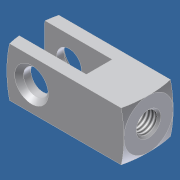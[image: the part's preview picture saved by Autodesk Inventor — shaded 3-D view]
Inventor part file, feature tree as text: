
AUTODESK INVENTOR PART (.ipt)
format: ipt  version: 2012 (Build 160160000, 160)  size: 169,984 bytes
history: native  units: in
note: dims shown in document units (in); Inventor stores cm internally (conversion verified against a paired STEP export)
features: other x126, sketch x7, revolve x5, extrude x2, thread x1
ambient origin geometry x8: Origin, YZ Plane, XZ Plane, XY Plane, X Axis, Y Axis, Z Axis, Center Point
bodies: Solid1 (feature_tree)
feature tree (141):
  extrude  "Extrusion1"  Depth=0.5in TaperAngle=0.0deg
  extrude  "Extrusion2"  Depth=0.44in TaperAngle=0.0deg
  revolve  "Revolution1"  Angle=360.0deg
  thread  "Thread1"  [1 undecoded]
  revolve  "Revolution2"  [1 undecoded]
  revolve  "Revolution3"  [1 undecoded]
  revolve  "Revolution4"  [1 undecoded]
  revolve  "Revolution5"  [1 undecoded]
  other  "th1_XY"
  other  "th1_YZ"
  other  "th1_ZX"
  other  "th1_X"
  other  "th1_Y"
  other  "th1_Z"
  other  "th1_Center"
  other  "th2_XY"
  other  "th2_YZ"
  other  "th2_ZX"
  other  "th2_X"
  other  "th2_Y"
  other  "th2_Z"
  other  "th2_Center"
  other  "rod_clevis_body_XY"
  other  "rod_clevis_body_YZ"
  other  "rod_clevis_body_ZX"
  other  "rod_clevis_body_X"
  other  "rod_clevis_body_Y"
  other  "rod_clevis_body_Z"
  other  "rod_clevis_body_Center"
  other  "piston_rod_clevis_XY"
  other  "piston_rod_clevis_YZ"
  other  "piston_rod_clevis_ZX"
  other  "piston_rod_clevis_X"
  other  "piston_rod_clevis_Y"
  other  "piston_rod_clevis_Z"
  other  "piston_rod_clevis_Center"
  other  "dummy_XY"
  other  "dummy_YZ"
  other  "dummy_ZX"
  other  "dummy_X"
  other  "dummy_Y"
  other  "dummy_Z"
  other  "dummy_Center"
  other  "l11_XY"
  other  "l11_YZ"
  other  "l11_ZX"
  other  "l11_X"
  other  "l11_Y"
  other  "l11_Z"
  other  "l11_Center"
  other  "l12_XY"
  other  "l12_YZ"
  other  "l12_ZX"
  other  "l12_X"
  other  "l12_Y"
  other  "l12_Z"
  other  "l12_Center"
  other  "l1_XY"
  other  "l1_YZ"
  other  "l1_ZX"
  other  "l1_X"
  other  "l1_Y"
  other  "l1_Z"
  other  "l1_Center"
  other  "h1_XY"
  other  "h1_YZ"
  other  "h1_ZX"
  other  "h1_X"
  other  "h1_Y"
  other  "h1_Z"
  other  "h1_Center"
  other  "l2_XY"
  other  "l2_YZ"
  other  "l2_ZX"
  other  "l2_X"
  other  "l2_Y"
  other  "l2_Z"
  other  "l2_Center"
  other  "h2_XY"
  other  "h2_YZ"
  other  "h2_ZX"
  other  "h2_X"
  other  "h2_Y"
  other  "h2_Z"
  other  "h2_Center"
  other  "w11_XY"
  other  "w11_YZ"
  other  "w11_ZX"
  other  "w11_X"
  other  "w11_Y"
  other  "w11_Z"
  other  "w11_Center"
  other  "w12_XY"
  other  "w12_YZ"
  other  "w12_ZX"
  other  "w12_X"
  other  "w12_Y"
  other  "w12_Z"
  other  "w12_Center"
  other  "l21_XY"
  other  "l21_YZ"
  other  "l21_ZX"
  other  "l21_X"
  other  "l21_Y"
  other  "l21_Z"
  other  "l21_Center"
  other  "l22_XY"
  other  "l22_YZ"
  other  "l22_ZX"
  other  "l22_X"
  other  "l22_Y"
  other  "l22_Z"
  other  "l22_Center"
  other  "w1_XY"
  other  "w1_YZ"
  other  "w1_ZX"
  other  "w1_X"
  other  "w1_Y"
  other  "w1_Z"
  other  "w1_Center"
  other  "w2_XY"
  other  "w2_YZ"
  other  "w2_ZX"
  other  "w2_X"
  other  "w2_Y"
  other  "w2_Z"
  other  "w2_Center"
  other  "to_cylinder_XY"
  other  "to_cylinder_YZ"
  other  "to_cylinder_ZX"
  other  "to_cylinder_X"
  other  "to_cylinder_Y"
  other  "to_cylinder_Z"
  other  "to_cylinder_Center"
  sketch  "Sketch_1"  dims[d0=0.5in d1=0.0in d2=0.5in d3=0.0in]
  sketch  "Sketch_2"  dims[d4=360.0deg d5=0.44in d6=0.0in]
  sketch  "Sketch_3"  dims[d7=360.0deg d8=360.0deg d9=360.0deg]
  sketch  "Sketch_4"  dims[d10=360.0deg]
  sketch  "Sketch_5"
  sketch  "Sketch_9"
  sketch  "Sketch_10"
note: 5 required parameter values undecoded (feature->parameter linkage not recoverable at this tier; creation-order binding heuristic only, values carry confidence <= 0.55)
